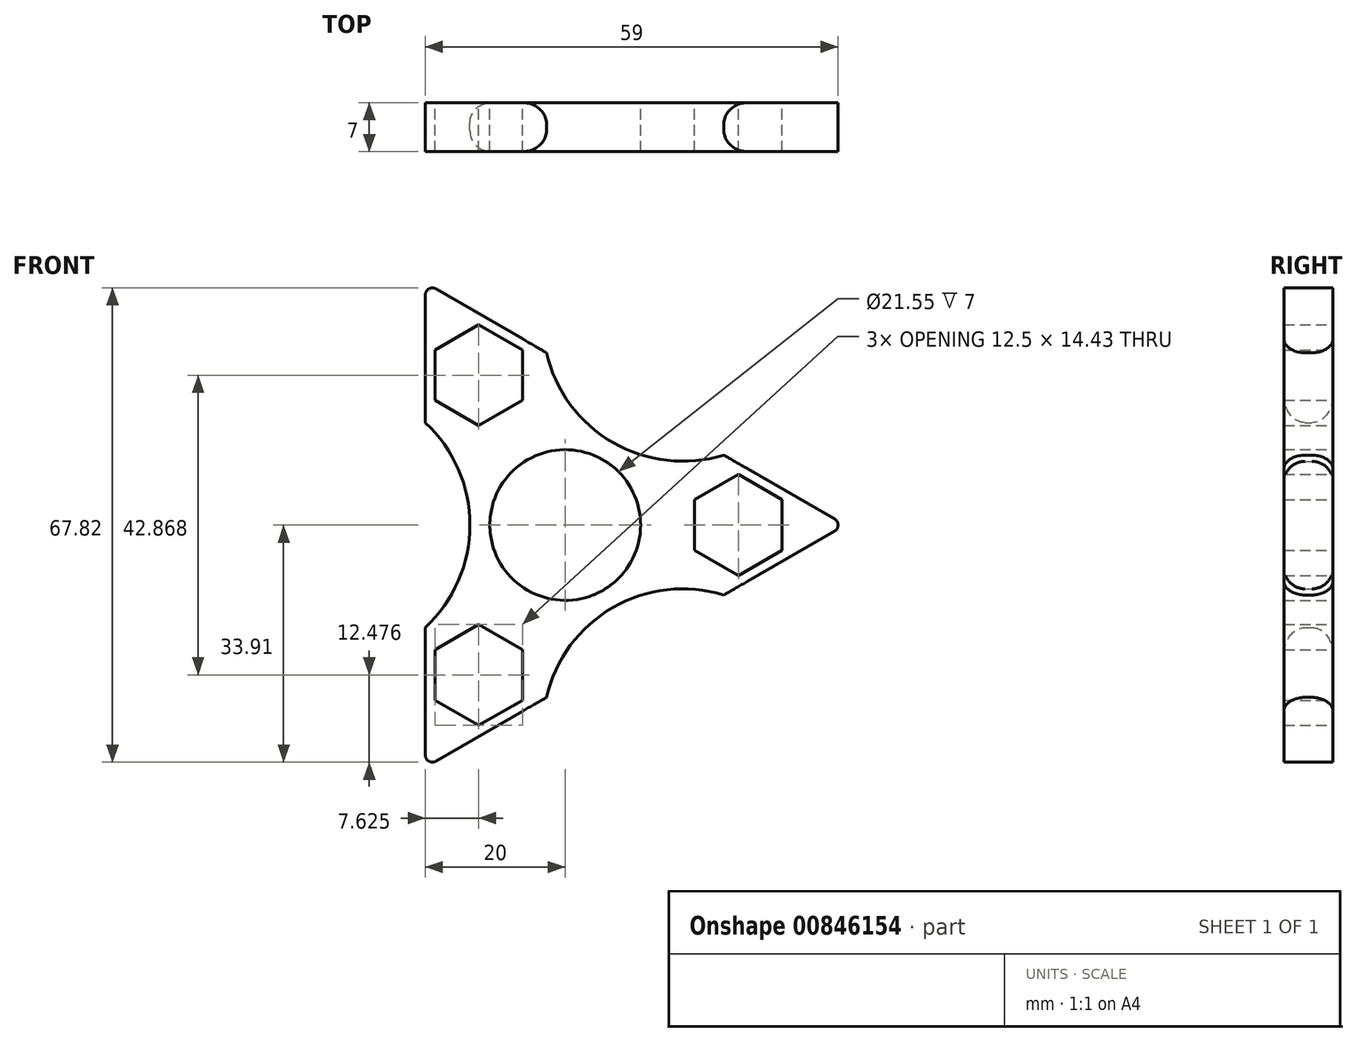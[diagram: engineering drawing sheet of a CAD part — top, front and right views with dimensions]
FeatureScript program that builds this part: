
annotation { "Feature Type Name" : "Feature", "Feature Type Description" : "" }
export const myFeature = defineFeature(function(context is Context, id is Id, definition is map)
    precondition{}
    {
        {
            var Q0;
            Q0=qCreatedBy(makeId("Front.planeOp"),FACE);
            var sketch = newSketch(context, id + "F0", { "sketchPlane" : qUnion([Q0])});
            skLineSegment(sketch, "E0", {"start": v(-60, 34.64) * mm, "end": v(-60, -34.64) * mm});
            skLineSegment(sketch, "E1", {"start": v(-60, -34.64) * mm, "end": v(0, 0) * mm});
            skLineSegment(sketch, "E2", {"start": v(0, 0) * mm, "end": v(-60, 34.64) * mm});
            skCircle(sketch, "E3.cCircle", {"center": v(-52.38, 21.43) * mm, "radius": 6.25 * mm, "construction": true});
            skLineSegment(sketch, "E3.0", {"start": v(-52.38, 14.22) * mm, "end": v(-58.63, 17.83) * mm});
            skLineSegment(sketch, "E3.1", {"start": v(-58.63, 17.83) * mm, "end": v(-58.63, 25.04) * mm});
            skLineSegment(sketch, "E3.2", {"start": v(-58.62, 25.04) * mm, "end": v(-52.37, 28.65) * mm});
            skLineSegment(sketch, "E3.3", {"start": v(-52.37, 28.65) * mm, "end": v(-46.13, 25.04) * mm});
            skLineSegment(sketch, "E3.4", {"start": v(-46.13, 25.04) * mm, "end": v(-46.13, 17.83) * mm});
            skLineSegment(sketch, "E3.5", {"start": v(-46.13, 17.83) * mm, "end": v(-52.38, 14.22) * mm});
            skPoint(sketch, "E3.0.midPoint", {"position": v(-55.5, 16.02) * mm});
            skLineSegment(sketch, "E4", {"start": v(-60, 34.64) * mm, "end": v(-30, -17.32) * mm, "construction": true});
            skLineSegment(sketch, "E5", {"start": v(0, 0) * mm, "end": v(-60, 0) * mm, "construction": true});
            skCircle(sketch, "E6.cCircle", {"center": v(-15.25, 0) * mm, "radius": 6.25 * mm, "construction": true});
            skLineSegment(sketch, "E6.0", {"start": v(-21.5, -3.6) * mm, "end": v(-21.5, 3.6) * mm});
            skLineSegment(sketch, "E6.1", {"start": v(-21.5, 3.6) * mm, "end": v(-15.25, 7.22) * mm});
            skLineSegment(sketch, "E6.2", {"start": v(-15.25, 7.22) * mm, "end": v(-9, 3.6) * mm});
            skLineSegment(sketch, "E6.3", {"start": v(-9, 3.6) * mm, "end": v(-9, -3.6) * mm});
            skLineSegment(sketch, "E6.4", {"start": v(-9, -3.6) * mm, "end": v(-15.25, -7.22) * mm});
            skLineSegment(sketch, "E6.5", {"start": v(-15.25, -7.22) * mm, "end": v(-21.5, -3.6) * mm});
            skPoint(sketch, "E6.0.midPoint", {"position": v(-21.5, 0) * mm});
            skLineSegment(sketch, "E7", {"start": v(-60, -34.64) * mm, "end": v(-30, 17.32) * mm, "construction": true});
            skCircle(sketch, "E8.cCircle", {"center": v(-52.37, -21.43) * mm, "radius": 6.25 * mm, "construction": true});
            skLineSegment(sketch, "E8.0", {"start": v(-52.37, -28.65) * mm, "end": v(-58.62, -25.04) * mm});
            skLineSegment(sketch, "E8.1", {"start": v(-58.62, -25.04) * mm, "end": v(-58.62, -17.83) * mm});
            skLineSegment(sketch, "E8.2", {"start": v(-58.62, -17.83) * mm, "end": v(-52.37, -14.22) * mm});
            skLineSegment(sketch, "E8.3", {"start": v(-52.37, -14.22) * mm, "end": v(-46.12, -17.83) * mm});
            skLineSegment(sketch, "E8.4", {"start": v(-46.12, -17.83) * mm, "end": v(-46.12, -25.04) * mm});
            skLineSegment(sketch, "E8.5", {"start": v(-46.12, -25.04) * mm, "end": v(-52.37, -28.65) * mm});
            skPoint(sketch, "E8.0.midPoint", {"position": v(-55.5, -26.85) * mm});
            skArc(sketch, "E9", {"start": v(-42.68, 24.64) * mm, "mid": v(-33.19, 11.8) * mm, "end": v(-17.32, 10) * mm});
            skArc(sketch, "E10", {"start": v(-60, -14.64) * mm, "mid": v(-53.63, 0) * mm, "end": v(-60, 14.64) * mm});
            skArc(sketch, "E11", {"start": v(-17.32, -10) * mm, "mid": v(-33.19, -11.8) * mm, "end": v(-42.68, -24.64) * mm});
            skSolve(sketch);
        }
        {
            var Q0;
            Q0=makeQuery(id+"F0.imprint","IMPRINT",FACE,{"disambiguationData":[TD([[makeQuery(id+"F0.imprint","IMPRINT",EDGE,{"derivedFrom":sQuery(id+"F0.wireOp",EDGE,"E3.0")}),1.0]])]});
            extrude(context, id + "F1", {"entities" : qUnion([Q0]), "depth" : 7 * mm, "offsetDistance" : 25 * mm});
        }
        {
            var Q0;
            Q0=makeQuery(id+"F1.opExtrude","SWEPT_EDGE",EDGE,{"disambiguationData":[OSD([sQuery(id+"F0.wireOp",EDGE,"E0"),sQuery(id+"F0.wireOp",EDGE,"E2")])]});
            var Q1;
            Q1=makeQuery(id+"F1.opExtrude","SWEPT_EDGE",EDGE,{"disambiguationData":[OSD([sQuery(id+"F0.wireOp",EDGE,"E0"),sQuery(id+"F0.wireOp",EDGE,"E1")])]});
            var Q2;
            Q2=makeQuery(id+"F1.opExtrude","SWEPT_EDGE",EDGE,{"disambiguationData":[OSD([sQuery(id+"F0.wireOp",EDGE,"E1"),sQuery(id+"F0.wireOp",EDGE,"E2")])]});
            fillet(context, id + "F2", {"entities" : qUnion([Q0, Q1, Q2]), "radius" : 1 * mm, "tangentPropagation" : true, "allowEdgeOverflow" : false});
        }
        {
            var Q0;
            Q0=makeQuery(id+"F1.opExtrude","CAP_EDGE",EDGE,{"disambiguationData":[OSD([sQuery(id+"F0.wireOp",EDGE,"E10")])],"isStart":true});
            var Q1;
            Q1=makeQuery(id+"F1.opExtrude","CAP_EDGE",EDGE,{"disambiguationData":[OSD([sQuery(id+"F0.wireOp",EDGE,"E10")])],"isStart":false});
            var Q2;
            Q2=makeQuery(id+"F1.opExtrude","CAP_EDGE",EDGE,{"disambiguationData":[OSD([sQuery(id+"F0.wireOp",EDGE,"E9")])],"isStart":false});
            var Q3;
            Q3=makeQuery(id+"F1.opExtrude","CAP_EDGE",EDGE,{"disambiguationData":[OSD([sQuery(id+"F0.wireOp",EDGE,"E11")])],"isStart":false});
            var Q4;
            Q4=makeQuery(id+"F1.opExtrude","CAP_EDGE",EDGE,{"disambiguationData":[OSD([sQuery(id+"F0.wireOp",EDGE,"E11")])],"isStart":true});
            var Q5;
            Q5=makeQuery(id+"F1.opExtrude","CAP_EDGE",EDGE,{"disambiguationData":[OSD([sQuery(id+"F0.wireOp",EDGE,"E9")])],"isStart":true});
            fillet(context, id + "F3", {"entities" : qUnion([Q0, Q1, Q2, Q3, Q4, Q5]), "radius" : 3 * mm, "tangentPropagation" : true, "allowEdgeOverflow" : false});
        }
        {
            var Q0;
            Q0=qCreatedBy(makeId("Front.planeOp"),FACE);
            var sketch = newSketch(context, id + "F4", { "sketchPlane" : qUnion([Q0])});
            skCircle(sketch, "E12", {"center": v(-40, 0) * mm, "radius": 10.78 * mm});
            skPoint(sketch, "E13.0", {"position": v(-59.5, 33.77) * mm});
            skPoint(sketch, "E14.0", {"position": v(-34.69, -9.2) * mm});
            skPoint(sketch, "E15.0", {"position": v(-50.63, 0) * mm});
            skLineSegment(sketch, "E16", {"start": v(0, 0) * mm, "end": v(-50.63, 0) * mm, "construction": true});
            skLineSegment(sketch, "E17", {"start": v(-59.5, 33.77) * mm, "end": v(-34.69, -9.2) * mm, "construction": true});
            skPoint(sketch, "E18.0", {"position": v(-34.69, 9.2) * mm});
            skPoint(sketch, "E19.0", {"position": v(-59.5, -33.77) * mm});
            skLineSegment(sketch, "E20", {"start": v(-59.5, -33.77) * mm, "end": v(-34.69, 9.2) * mm, "construction": true});
            skSolve(sketch);
        }
        {
            var Q0;
            Q0=makeQuery(id+"F4.imprint","IMPRINT",FACE,{"disambiguationData":[TD([[makeQuery(id+"F4.imprint","IMPRINT",EDGE,{"derivedFrom":sQuery(id+"F4.wireOp",EDGE,"E12")}),1.0]])]});
            extrude(context, id + "F5", {"entities" : qUnion([Q0]), "operationType" : NewBodyOperationType.REMOVE, "endBound" : BoundingType.SYMMETRIC, "depth" : 25 * mm, "offsetDistance" : 25 * mm});
        }
    });
